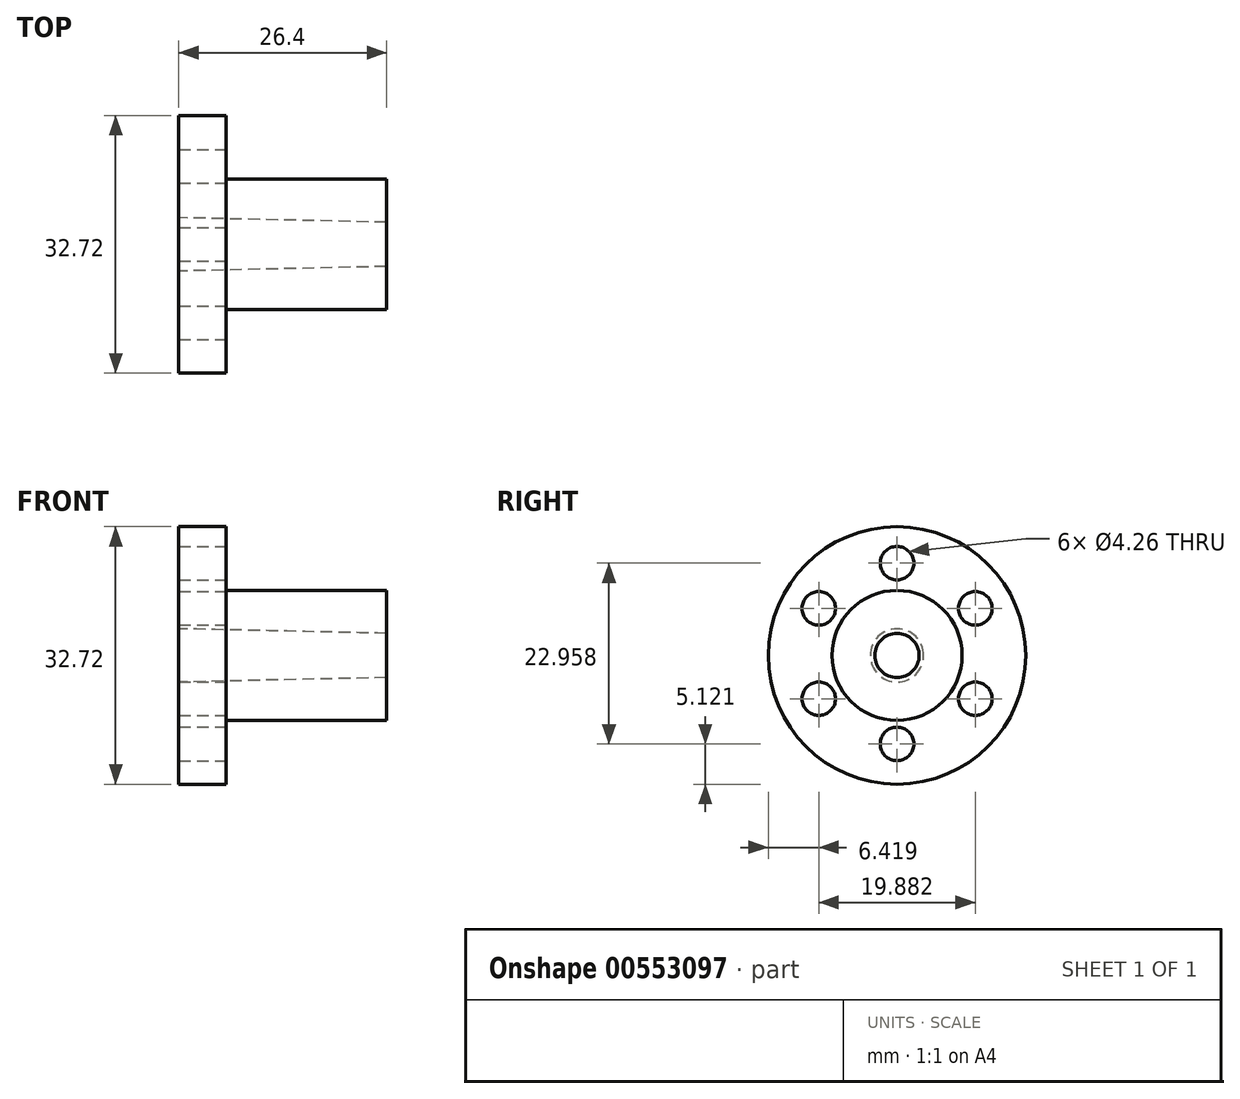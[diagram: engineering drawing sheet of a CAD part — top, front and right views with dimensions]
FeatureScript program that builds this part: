
annotation { "Feature Type Name" : "Feature", "Feature Type Description" : "" }
export const myFeature = defineFeature(function(context is Context, id is Id, definition is map)
    precondition{}
    {
        {
            var Q0;
            Q0=qCreatedBy(makeId("Front.planeOp"),FACE);
            var sketch = newSketch(context, id + "F0", { "sketchPlane" : qUnion([Q0])});
            skLineSegment(sketch, "E0", {"start": v(-11.55, 16.12) * mm, "end": v(-5.55, 16.12) * mm});
            skLineSegment(sketch, "E1", {"start": v(-5.55, 16.12) * mm, "end": v(-5.55, 8.02) * mm});
            skLineSegment(sketch, "E2", {"start": v(-5.55, 8.02) * mm, "end": v(14.85, 8.02) * mm});
            skLineSegment(sketch, "E3", {"start": v(14.85, 8.02) * mm, "end": v(14.85, 2.57) * mm});
            skLineSegment(sketch, "E4", {"start": v(14.85, 2.57) * mm, "end": v(-11.55, 3.14) * mm});
            skLineSegment(sketch, "E5", {"start": v(-11.55, 3.14) * mm, "end": v(-11.55, 16.12) * mm});
            skLineSegment(sketch, "E6", {"start": v(-17.06, -0.24) * mm, "end": v(17.32, -0.24) * mm});
            skSolve(sketch);
        }
        {
            var Q0;
            Q0=makeQuery(id+"F0.imprint","IMPRINT",FACE,{"disambiguationData":[TD([[makeQuery(id+"F0.imprint","IMPRINT",EDGE,{"derivedFrom":sQuery(id+"F0.wireOp",EDGE,"E0")}),-1.0]])]});
            var Q1;
            Q1=sQuery(id+"F0.wireOp",EDGE,"E6");
            revolve(context, id + "F1", {"entities" : qUnion([Q0]), "axis" : qUnion([Q1]), "revolveType" : RevolveType.FULL});
        }
        {
            var Q0;
            Q0=makeQuery(id+"F1.opRevolve","SWEPT_FACE",FACE,{"disambiguationData":[OSD([sQuery(id+"F0.wireOp",EDGE,"E1")])]});
            var sketch = newSketch(context, id + "F2", { "sketchPlane" : qUnion([Q0])});
            skLineSegment(sketch, "E7", {"start": v(0, 0) * mm, "end": v(0, 16.12) * mm, "construction": true});
            skCircle(sketch, "E8", {"center": v(0, 11.48) * mm, "radius": 2.13 * mm});
            skCircle(sketch, "E9.1.0", {"center": v(-9.94, 5.74) * mm, "radius": 2.13 * mm});
            skCircle(sketch, "E9.2.0", {"center": v(-9.94, -5.74) * mm, "radius": 2.13 * mm});
            skCircle(sketch, "E9.3.0", {"center": v(0, -11.48) * mm, "radius": 2.13 * mm});
            skCircle(sketch, "E9.4.0", {"center": v(9.94, -5.74) * mm, "radius": 2.13 * mm});
            skCircle(sketch, "E9.5.0", {"center": v(9.94, 5.74) * mm, "radius": 2.13 * mm});
            skPoint(sketch, "E9.center", {"position": v(0, 0) * mm});
            skSolve(sketch);
        }
        {
            var Q0;
            Q0=makeQuery(id+"F2.imprint","IMPRINT",FACE,{"disambiguationData":[TD([[makeQuery(id+"F2.imprint","IMPRINT",EDGE,{"derivedFrom":sQuery(id+"F2.wireOp",EDGE,"E9.1.0")}),1.0]])]});
            var Q1;
            Q1=makeQuery(id+"F2.imprint","IMPRINT",FACE,{"disambiguationData":[TD([[makeQuery(id+"F2.imprint","IMPRINT",EDGE,{"derivedFrom":sQuery(id+"F2.wireOp",EDGE,"E9.2.0")}),1.0]])]});
            var Q2;
            Q2=makeQuery(id+"F2.imprint","IMPRINT",FACE,{"disambiguationData":[TD([[makeQuery(id+"F2.imprint","IMPRINT",EDGE,{"derivedFrom":sQuery(id+"F2.wireOp",EDGE,"E9.3.0")}),1.0]])]});
            var Q3;
            Q3=makeQuery(id+"F2.imprint","IMPRINT",FACE,{"disambiguationData":[TD([[makeQuery(id+"F2.imprint","IMPRINT",EDGE,{"derivedFrom":sQuery(id+"F2.wireOp",EDGE,"E9.4.0")}),1.0]])]});
            var Q4;
            Q4=makeQuery(id+"F2.imprint","IMPRINT",FACE,{"disambiguationData":[TD([[makeQuery(id+"F2.imprint","IMPRINT",EDGE,{"derivedFrom":sQuery(id+"F2.wireOp",EDGE,"E9.5.0")}),1.0]])]});
            var Q5;
            Q5=makeQuery(id+"F2.imprint","IMPRINT",FACE,{"disambiguationData":[TD([[makeQuery(id+"F2.imprint","IMPRINT",EDGE,{"derivedFrom":sQuery(id+"F2.wireOp",EDGE,"E8")}),1.0]])]});
            extrude(context, id + "F3", {"entities" : qUnion([Q0, Q1, Q2, Q3, Q4, Q5]), "operationType" : NewBodyOperationType.REMOVE, "endBound" : BoundingType.THROUGH_ALL, "oppositeDirection" : true, "depth" : 25 * mm, "offsetDistance" : 25 * mm});
        }
    });
